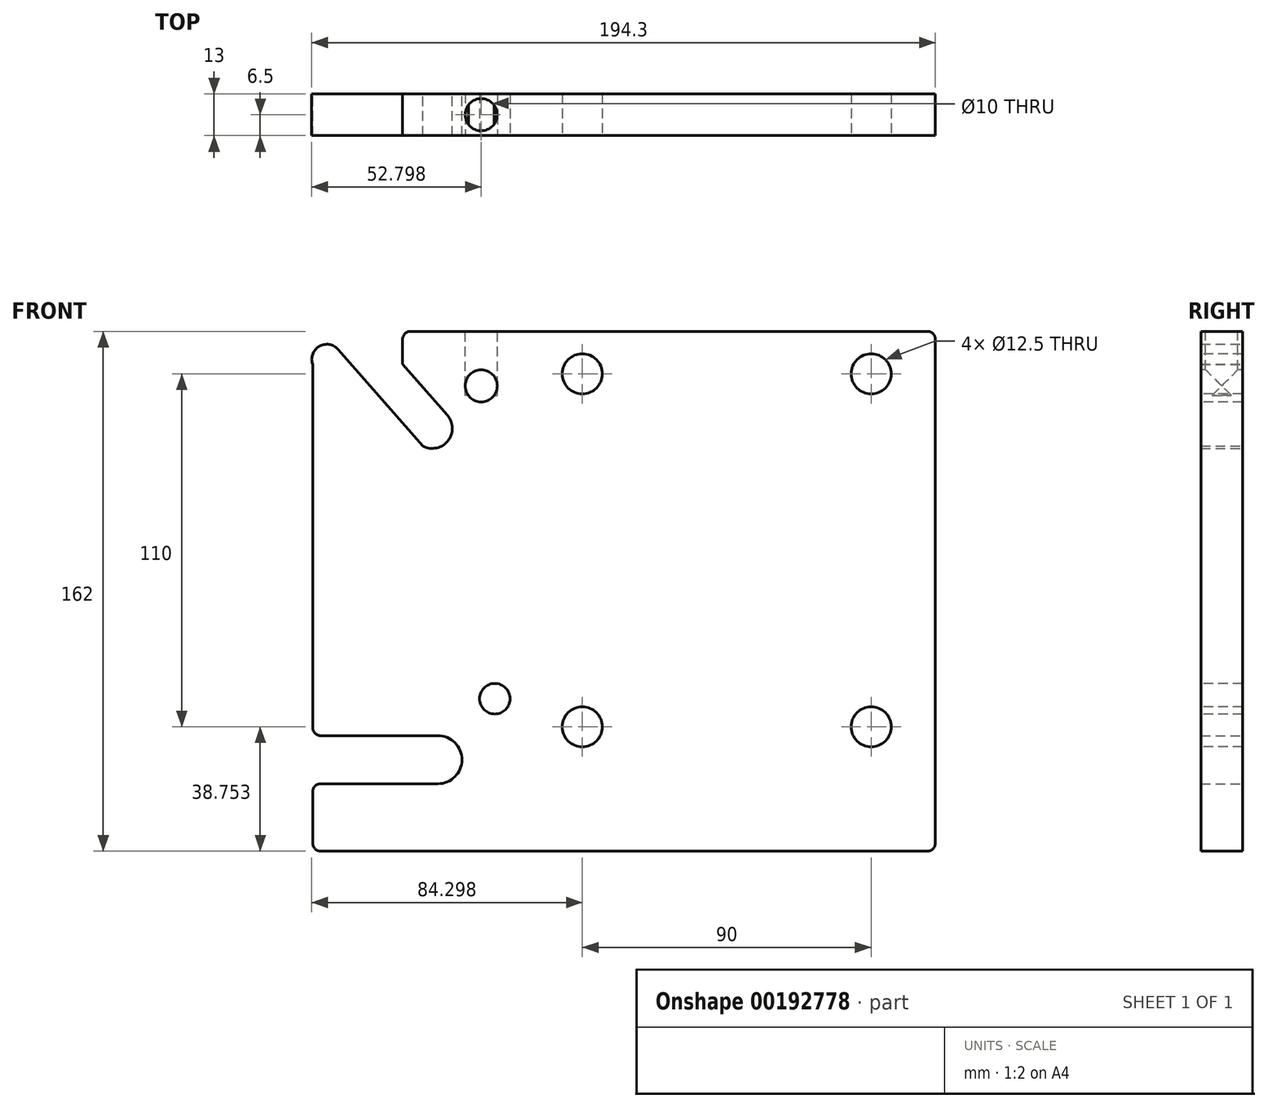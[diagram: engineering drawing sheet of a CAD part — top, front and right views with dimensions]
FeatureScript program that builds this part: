
annotation { "Feature Type Name" : "Feature", "Feature Type Description" : "" }
export const myFeature = defineFeature(function(context is Context, id is Id, definition is map)
    precondition{}
    {
        {
            var Q0;
            Q0=qCreatedBy(makeId("Front.planeOp"),FACE);
            var sketch = newSketch(context, id + "F0", { "sketchPlane" : qUnion([Q0])});
            skLineSegment(sketch, "E0", {"start": v(-64.11, -104.19) * mm, "end": v(-64.11, -88.19) * mm});
            skLineSegment(sketch, "E1", {"start": v(-61.61, -85.69) * mm, "end": v(-25.11, -85.69) * mm});
            skLineSegment(sketch, "E2", {"start": v(-25.11, -70.69) * mm, "end": v(-53.58, -70.69) * mm});
            skLineSegment(sketch, "E3", {"start": v(-64.11, -36.54) * mm, "end": v(-64.11, 44.95) * mm});
            skLineSegment(sketch, "E4", {"start": v(-56.2, 49.67) * mm, "end": v(-29.74, 19.51) * mm});
            skLineSegment(sketch, "E5", {"start": v(-22.16, 29.19) * mm, "end": v(-36.11, 45.08) * mm});
            skLineSegment(sketch, "E6", {"start": v(-36.11, 45.08) * mm, "end": v(-36.11, 52.81) * mm});
            skLineSegment(sketch, "E7", {"start": v(-33.61, 55.31) * mm, "end": v(127.39, 55.31) * mm});
            skLineSegment(sketch, "E8", {"start": v(129.89, 52.81) * mm, "end": v(129.89, -104.19) * mm});
            skLineSegment(sketch, "E9", {"start": v(127.39, -106.69) * mm, "end": v(-61.61, -106.69) * mm});
            skArc(sketch, "E10", {"start": v(-25.11, -85.69) * mm, "mid": v(-17.61, -78.19) * mm, "end": v(-25.11, -70.69) * mm});
            skArc(sketch, "E11", {"start": v(-56.2, 49.67) * mm, "mid": v(-62.12, 50.6) * mm, "end": v(-64.11, 44.95) * mm});
            skArc(sketch, "E12", {"start": v(-29.74, 19.51) * mm, "mid": v(-21.94, 21.21) * mm, "end": v(-22.16, 29.19) * mm});
            skPoint(sketch, "E13.visualSharp", {"position": v(-36.11, 55.31) * mm});
            skArc(sketch, "E13.filletArc", {"start": v(-33.61, 55.31) * mm, "mid": v(-35.38, 54.58) * mm, "end": v(-36.11, 52.81) * mm});
            skPoint(sketch, "E14.visualSharp", {"position": v(129.89, 55.31) * mm});
            skArc(sketch, "E14.filletArc", {"start": v(129.89, 52.81) * mm, "mid": v(129.16, 54.58) * mm, "end": v(127.39, 55.31) * mm});
            skPoint(sketch, "E15.visualSharp", {"position": v(129.89, -106.69) * mm});
            skArc(sketch, "E15.filletArc", {"start": v(127.39, -106.69) * mm, "mid": v(129.16, -105.96) * mm, "end": v(129.89, -104.19) * mm});
            skPoint(sketch, "E16.visualSharp", {"position": v(-64.11, -106.69) * mm});
            skArc(sketch, "E16.filletArc", {"start": v(-64.11, -104.19) * mm, "mid": v(-63.38, -105.96) * mm, "end": v(-61.61, -106.69) * mm});
            skLineSegment(sketch, "E17", {"start": v(-53.58, -70.69) * mm, "end": v(-61.61, -70.69) * mm});
            skLineSegment(sketch, "E18", {"start": v(-64.11, -68.19) * mm, "end": v(-64.11, -36.54) * mm});
            skPoint(sketch, "E19.visualSharp", {"position": v(-64.11, -70.69) * mm});
            skArc(sketch, "E19.filletArc", {"start": v(-64.11, -68.19) * mm, "mid": v(-63.38, -69.96) * mm, "end": v(-61.61, -70.69) * mm});
            skPoint(sketch, "E20.visualSharp", {"position": v(-64.11, -85.69) * mm});
            skArc(sketch, "E20.filletArc", {"start": v(-61.61, -85.69) * mm, "mid": v(-63.38, -86.42) * mm, "end": v(-64.11, -88.19) * mm});
            skSolve(sketch);
        }
        {
            var Q0;
            Q0=makeQuery(id+"F0.imprint","IMPRINT",FACE,{"disambiguationData":[TD([[makeQuery(id+"F0.imprint","IMPRINT",EDGE,{"derivedFrom":sQuery(id+"F0.wireOp",EDGE,"E0")}),-1.0]])]});
            extrude(context, id + "F1", {"entities" : qUnion([Q0]), "depth" : 13 * mm});
        }
        {
            var Q0;
            Q0=makeQuery(id+"F1.opExtrude","CAP_FACE",FACE,{"disambiguationData":[OSD([sQuery(id+"F0.wireOp",EDGE,"E0"),sQuery(id+"F0.wireOp",EDGE,"E1"),sQuery(id+"F0.wireOp",EDGE,"E2"),sQuery(id+"F0.wireOp",EDGE,"E3"),sQuery(id+"F0.wireOp",EDGE,"E4"),sQuery(id+"F0.wireOp",EDGE,"E5"),sQuery(id+"F0.wireOp",EDGE,"E6"),sQuery(id+"F0.wireOp",EDGE,"E7"),sQuery(id+"F0.wireOp",EDGE,"E8"),sQuery(id+"F0.wireOp",EDGE,"E9"),sQuery(id+"F0.wireOp",EDGE,"E10"),sQuery(id+"F0.wireOp",EDGE,"E11"),sQuery(id+"F0.wireOp",EDGE,"E12"),sQuery(id+"F0.wireOp",EDGE,"E13.filletArc"),sQuery(id+"F0.wireOp",EDGE,"E14.filletArc"),sQuery(id+"F0.wireOp",EDGE,"E15.filletArc"),sQuery(id+"F0.wireOp",EDGE,"E16.filletArc"),sQuery(id+"F0.wireOp",EDGE,"E17"),sQuery(id+"F0.wireOp",EDGE,"E18"),sQuery(id+"F0.wireOp",EDGE,"E19.filletArc"),sQuery(id+"F0.wireOp",EDGE,"E20.filletArc")])],"isStart":false});
            var sketch = newSketch(context, id + "F2", { "sketchPlane" : qUnion([Q0])});
            skCircle(sketch, "E21", {"center": v(109.89, 42.06) * mm, "radius": 6.25 * mm});
            skCircle(sketch, "E22", {"center": v(19.89, 42.06) * mm, "radius": 6.25 * mm});
            skCircle(sketch, "E23", {"center": v(-7.36, -59.19) * mm, "radius": 4.75 * mm});
            skCircle(sketch, "E24", {"center": v(19.89, -67.94) * mm, "radius": 6.25 * mm});
            skCircle(sketch, "E25", {"center": v(109.89, -67.94) * mm, "radius": 6.25 * mm});
            skCircle(sketch, "E26", {"center": v(-11.61, 38.31) * mm, "radius": 5 * mm});
            skSolve(sketch);
        }
        {
            var Q0;
            Q0=makeQuery(id+"F2.imprint","IMPRINT",FACE,{"disambiguationData":[TD([[makeQuery(id+"F2.imprint","IMPRINT",EDGE,{"derivedFrom":sQuery(id+"F2.wireOp",EDGE,"E26")}),1.0]])]});
            var Q1;
            Q1=makeQuery(id+"F2.imprint","IMPRINT",FACE,{"disambiguationData":[TD([[makeQuery(id+"F2.imprint","IMPRINT",EDGE,{"derivedFrom":sQuery(id+"F2.wireOp",EDGE,"E22")}),1.0]])]});
            var Q2;
            Q2=makeQuery(id+"F2.imprint","IMPRINT",FACE,{"disambiguationData":[TD([[makeQuery(id+"F2.imprint","IMPRINT",EDGE,{"derivedFrom":sQuery(id+"F2.wireOp",EDGE,"E21")}),1.0]])]});
            var Q3;
            Q3=makeQuery(id+"F2.imprint","IMPRINT",FACE,{"disambiguationData":[TD([[makeQuery(id+"F2.imprint","IMPRINT",EDGE,{"derivedFrom":sQuery(id+"F2.wireOp",EDGE,"E25")}),1.0]])]});
            var Q4;
            Q4=makeQuery(id+"F2.imprint","IMPRINT",FACE,{"disambiguationData":[TD([[makeQuery(id+"F2.imprint","IMPRINT",EDGE,{"derivedFrom":sQuery(id+"F2.wireOp",EDGE,"E24")}),1.0]])]});
            var Q5;
            Q5=makeQuery(id+"F2.imprint","IMPRINT",FACE,{"disambiguationData":[TD([[makeQuery(id+"F2.imprint","IMPRINT",EDGE,{"derivedFrom":sQuery(id+"F2.wireOp",EDGE,"E23")}),1.0]])]});
            extrude(context, id + "F3", {"entities" : qUnion([Q0, Q1, Q2, Q3, Q4, Q5]), "operationType" : NewBodyOperationType.REMOVE, "oppositeDirection" : true, "depth" : 13 * mm});
        }
        {
            var Q0;
            Q0=makeQuery(id+"F1.opExtrude","SWEPT_FACE",FACE,{"disambiguationData":[OSD([sQuery(id+"F0.wireOp",EDGE,"E7")])]});
            var sketch = newSketch(context, id + "F4", { "sketchPlane" : qUnion([Q0])});
            skCircle(sketch, "E27", {"center": v(-11.61, -6.5) * mm, "radius": 5 * mm});
            skSolve(sketch);
        }
        {
            var Q0;
            Q0=makeQuery(id+"F4.imprint","IMPRINT",FACE,{"disambiguationData":[TD([[makeQuery(id+"F4.imprint","IMPRINT",EDGE,{"derivedFrom":sQuery(id+"F4.wireOp",EDGE,"E27")}),1.0]])]});
            extrude(context, id + "F5", {"entities" : qUnion([Q0]), "operationType" : NewBodyOperationType.REMOVE, "oppositeDirection" : true, "depth" : 20 * mm});
        }
    });
